# Revit family: Kessel AG 93002.00D1R en
name_source: partatom
category: Plumbing Fixtures
revit_build: Autodesk Revit 2014 (Build: 20130308_1515(x64)
units: mm (PartAtom-declared; Revit-internal decimal feet)

## types (1)
- Kessel AG 93002.00D1R en
    <CIBSE-1033.20.21> Overall Length [mm] = Direct
    <CIBSE-1033.20.22> Overall Width [mm] = 200
    <CIBSE-1033.20.23> Overall Height [mm] = 400
    <CIBSE-1033.20.24> GrossWeight [kg] = 100
    <CIBSE-1033.8.10> Manufacturer Website [URL] = www.kessel.com
    <CIBSE-1033.8.11> Product Range [Text] = EasyClean Modular grease separator, NS 2, Direct, 2-piece
    <CIBSE-1033.8.12> Product Model Number  [Text] = 93002.00/D1-R
    <CIBSE-1033.8.14> Product Literature [URL] = http://www.kessel.de
    <CIBSE-1033.8.9> Manufacturer [Text] = Kessel AG
    CONNECTOR0_DIAMETER_dX_0r = 0 mm  [stored 0 ft]
    CONNECTOR0_dX_00 = 545 mm
    CONNECTOR0_dX_01 = 435 mm
    CONNECTOR0_ref_dX = 435 mm
    CONNECTOR0_ref_dZ = 1143 mm
    CONNECTOR1_DIAMETER_dX_0r = 0 mm  [stored 0 ft]
    CONNECTOR1_dX_00 = 435 mm
    CONNECTOR1_dX_01 = 545 mm
    CONNECTOR1_ref_dX = 435 mm
    CONNECTOR1_ref_dZ = 1073 mm
    CONNECTOR2_DIAMETER_dZ_0r = 0 mm  [stored 0 ft]
    CONNECTOR2_dZ_00 = 1110 mm
    CONNECTOR2_dZ_01 = 1160 mm
    CONNECTOR2_ref_dX = 429 mm
    CONNECTOR2_ref_dY = 429 mm
    CONNECTOR2_ref_dZ = 1110 mm
    Manufacturer = Kessel AG
    Model = 93002.00/D1-R
    URL = www.kessel.com

note: [stored X ft] marks values corroborated as IEEE doubles in the binary element streams (Revit-internal decimal feet)
